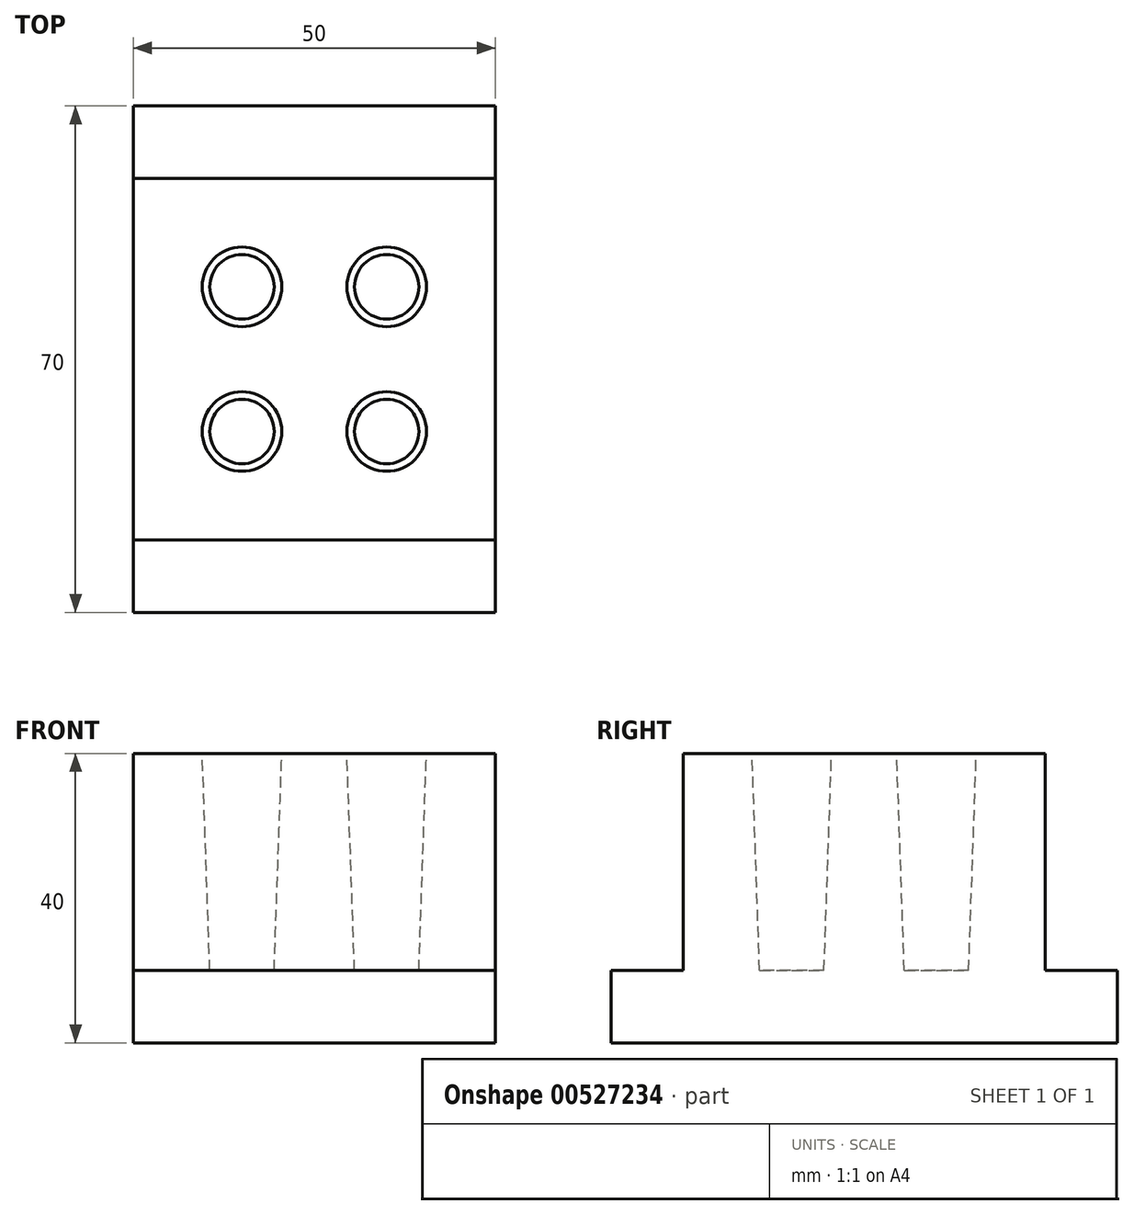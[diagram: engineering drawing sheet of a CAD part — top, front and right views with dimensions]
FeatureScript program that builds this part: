
annotation { "Feature Type Name" : "Feature", "Feature Type Description" : "" }
export const myFeature = defineFeature(function(context is Context, id is Id, definition is map)
    precondition{}
    {
        {
            var Q0;
            Q0=qCreatedBy(makeId("Top.planeOp"),FACE);
            var sketch = newSketch(context, id + "F0", { "sketchPlane" : qUnion([Q0])});
            skLineSegment(sketch, "E0.bottom", {"start": v(-25, 25) * mm, "end": v(25, 25) * mm});
            skLineSegment(sketch, "E0.top", {"start": v(-25, -25) * mm, "end": v(25, -25) * mm});
            skLineSegment(sketch, "E0.left", {"start": v(-25, 25) * mm, "end": v(-25, -25) * mm});
            skLineSegment(sketch, "E0.right", {"start": v(25, 25) * mm, "end": v(25, -25) * mm});
            skSolve(sketch);
        }
        {
            var Q0;
            Q0=makeQuery(id+"F0.imprint","IMPRINT",FACE,{"disambiguationData":[TD([[makeQuery(id+"F0.imprint","IMPRINT",EDGE,{"derivedFrom":sQuery(id+"F0.wireOp",EDGE,"E0.bottom")}),-1.0]])]});
            extrude(context, id + "F1", {"entities" : qUnion([Q0]), "depth" : 30 * mm, "offsetDistance" : 25 * mm});
        }
        {
            var Q0;
            Q0=qCreatedBy(makeId("Top.planeOp"),FACE);
            var sketch = newSketch(context, id + "F2", { "sketchPlane" : qUnion([Q0])});
            skCircle(sketch, "E1", {"center": v(10, 10) * mm, "radius": 4.45 * mm});
            skCircle(sketch, "E2", {"center": v(-10, 10) * mm, "radius": 4.45 * mm});
            skCircle(sketch, "E3", {"center": v(10, -10) * mm, "radius": 4.45 * mm});
            skCircle(sketch, "E4", {"center": v(-10, -10) * mm, "radius": 4.45 * mm});
            skLineSegment(sketch, "E5", {"start": v(45.6, 10) * mm, "end": v(-25.6, 10) * mm, "construction": true});
            skLineSegment(sketch, "E6", {"start": v(33, -10) * mm, "end": v(-38.2, -10) * mm, "construction": true});
            skLineSegment(sketch, "E7", {"start": v(-10, 29.67) * mm, "end": v(-10, -31.49) * mm, "construction": true});
            skLineSegment(sketch, "E8", {"start": v(10, 30.04) * mm, "end": v(10, -31.73) * mm, "construction": true});
            skSolve(sketch);
        }
        {
            var Q0;
            Q0 = qSketchRegion(id + "F2", true);
            extrude(context, id + "F3", {"entities" : qUnion([Q0]), "operationType" : NewBodyOperationType.REMOVE, "depth" : 30 * mm, "offsetDistance" : 25 * mm, "hasDraft" : true, "draftAngle" : 2 * degree});
        }
        {
            var Q0;
            Q0=qCreatedBy(makeId("Top.planeOp"),FACE);
            var sketch = newSketch(context, id + "F4", { "sketchPlane" : qUnion([Q0])});
            skLineSegment(sketch, "E9.bottom", {"start": v(-25, 35) * mm, "end": v(25, 35) * mm});
            skLineSegment(sketch, "E9.top", {"start": v(-25, -35) * mm, "end": v(25, -35) * mm});
            skLineSegment(sketch, "E9.left", {"start": v(-25, 35) * mm, "end": v(-25, -35) * mm});
            skLineSegment(sketch, "E9.right", {"start": v(25, 35) * mm, "end": v(25, -35) * mm});
            skSolve(sketch);
        }
        {
            var Q0;
            Q0=makeQuery(id+"F4.imprint","IMPRINT",FACE,{"disambiguationData":[TD([[makeQuery(id+"F4.imprint","IMPRINT",EDGE,{"derivedFrom":sQuery(id+"F4.wireOp",EDGE,"E9.bottom")}),-1.0]])]});
            extrude(context, id + "F5", {"entities" : qUnion([Q0]), "operationType" : NewBodyOperationType.ADD, "oppositeDirection" : true, "depth" : 10 * mm, "offsetDistance" : 25 * mm});
        }
    });
